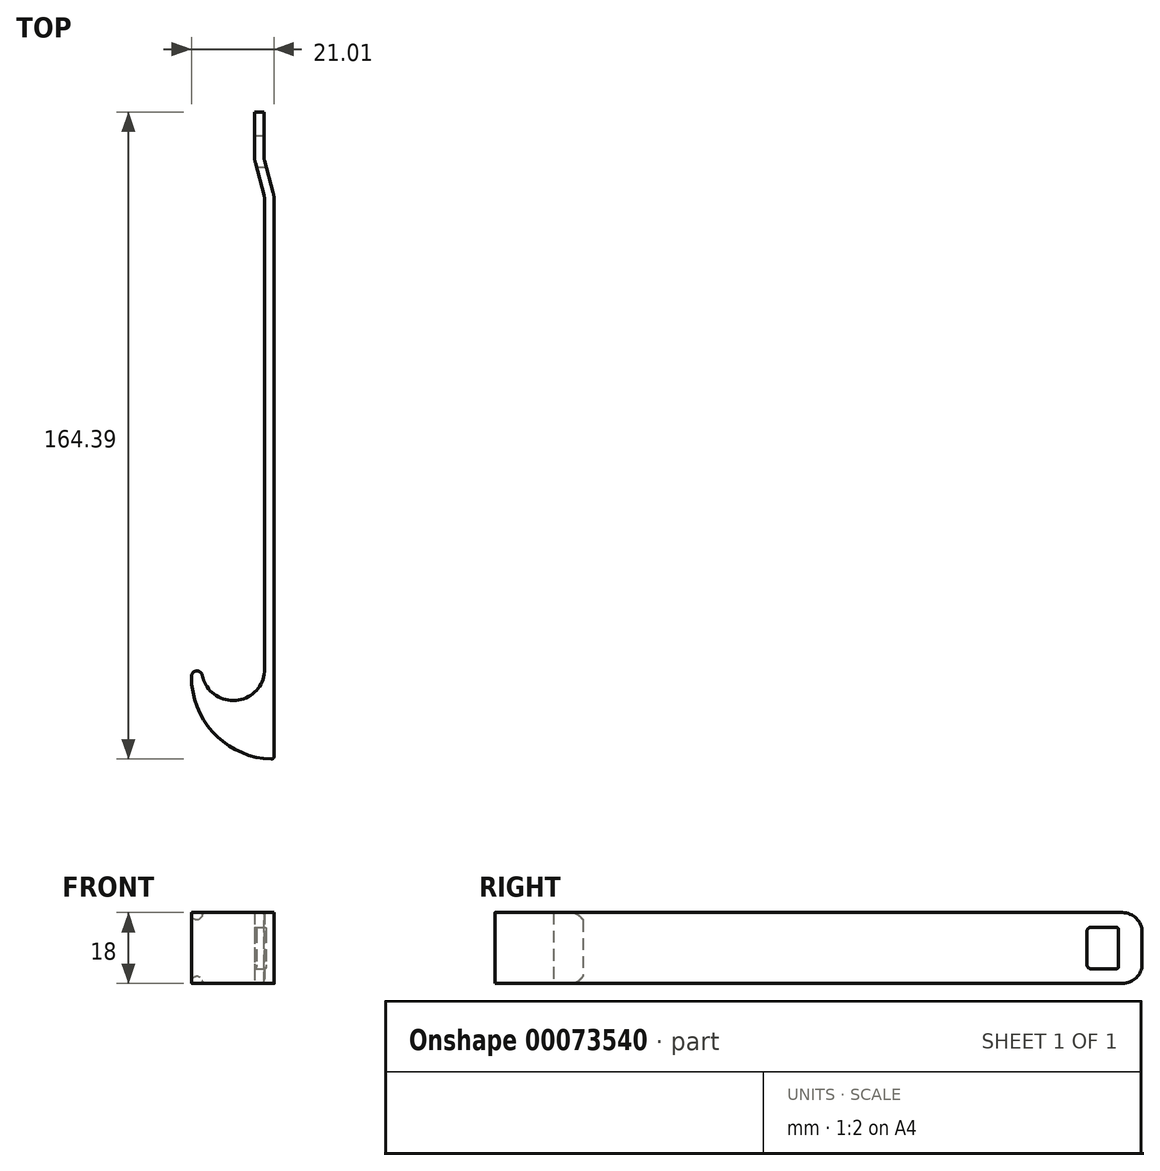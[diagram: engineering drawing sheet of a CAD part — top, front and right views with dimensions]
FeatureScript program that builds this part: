
annotation { "Feature Type Name" : "Feature", "Feature Type Description" : "" }
export const myFeature = defineFeature(function(context is Context, id is Id, definition is map)
    precondition{}
    {
        {
            var Q0;
            Q0=qCreatedBy(makeId("Top.planeOp"),FACE);
            var sketch = newSketch(context, id + "F0", { "sketchPlane" : qUnion([Q0])});
            skLineSegment(sketch, "E0", {"start": v(-2.4, -9.7) * mm, "end": v(-2.4, -129.5) * mm});
            skArc(sketch, "E1", {"start": v(-18.23, -131.12) * mm, "mid": v(-9.59, -137.46) * mm, "end": v(-2.4, -129.5) * mm});
            skLineSegment(sketch, "E2", {"start": v(-18.23, -131.12) * mm, "end": v(-10.4, -129.5) * mm, "construction": true});
            skLineSegment(sketch, "E3", {"start": v(-10.4, -129.5) * mm, "end": v(-2.4, -129.5) * mm, "construction": true});
            skArc(sketch, "E4", {"start": v(-18.23, -131.12) * mm, "mid": v(-19.75, -130) * mm, "end": v(-21, -131.4) * mm});
            skArc(sketch, "E5", {"start": v(-21, -131.4) * mm, "mid": v(-15.1, -146) * mm, "end": v(-0.72, -152.4) * mm});
            skLineSegment(sketch, "E6", {"start": v(0, -151.7) * mm, "end": v(0, -9.39) * mm});
            skLineSegment(sketch, "E7", {"start": v(-21, -131.4) * mm, "end": v(-21, -129.5) * mm, "construction": true});
            skLineSegment(sketch, "E8", {"start": v(-21, -129.5) * mm, "end": v(-10.4, -129.5) * mm, "construction": true});
            skPoint(sketch, "E9.visualSharp", {"position": v(0, -152.4) * mm});
            skArc(sketch, "E9.filletArc", {"start": v(-0.72, -152.4) * mm, "mid": v(-0.21, -152.2) * mm, "end": v(0, -151.7) * mm});
            skLineSegment(sketch, "E10", {"start": v(-21, -130) * mm, "end": v(-18.23, -130) * mm, "construction": true});
            skLineSegment(sketch, "E11", {"start": v(-18.23, -130) * mm, "end": v(-18.23, -131.12) * mm, "construction": true});
            skLineSegment(sketch, "E12", {"start": v(-5, 0) * mm, "end": v(-5, 12) * mm});
            skLineSegment(sketch, "E13", {"start": v(-5, 12) * mm, "end": v(-2.6, 12) * mm});
            skLineSegment(sketch, "E14", {"start": v(-2.6, 12) * mm, "end": v(-2.6, 0.32) * mm});
            skLineSegment(sketch, "E15", {"start": v(-0.72, -152.4) * mm, "end": v(0, -152.4) * mm, "construction": true});
            skLineSegment(sketch, "E16", {"start": v(0, -152.4) * mm, "end": v(0, -151.7) * mm, "construction": true});
            skPoint(sketch, "E17.visualSharp", {"position": v(0, 0) * mm});
            skLineSegment(sketch, "E18", {"start": v(-5, 0) * mm, "end": v(-2.4, -9.7) * mm});
            skLineSegment(sketch, "E19", {"start": v(-5, 0) * mm, "end": v(-2.52, 0) * mm, "construction": true});
            skLineSegment(sketch, "E20", {"start": v(-2.6, 0.32) * mm, "end": v(0, -9.39) * mm});
            skSolve(sketch);
        }
        {
            var Q0;
            Q0 = qSketchRegion(id + "F0", true);
            extrude(context, id + "F1", {"entities" : qUnion([Q0]), "depth" : 18 * mm, "symmetric" : true});
        }
        {
            var Q0;
            Q0=makeQuery(id+"F1.opExtrude","SWEPT_EDGE",EDGE,{"disambiguationData":[OSD([sQuery(id+"F0.wireOp",EDGE,"E0"),sQuery(id+"F0.wireOp",EDGE,"E18")])]});
            var Q1;
            Q1=makeQuery(id+"F1.opExtrude","SWEPT_EDGE",EDGE,{"disambiguationData":[OSD([sQuery(id+"F0.wireOp",EDGE,"E14"),sQuery(id+"F0.wireOp",EDGE,"E20")])]});
            fillet(context, id + "F2", {"entities" : qUnion([Q0, Q1]), "radius" : 5 * mm, "tangentPropagation" : true, "allowEdgeOverflow" : false});
        }
        {
            var Q0;
            Q0=makeQuery(id+"F1.opExtrude","SWEPT_EDGE",EDGE,{"disambiguationData":[OSD([sQuery(id+"F0.wireOp",EDGE,"E12"),sQuery(id+"F0.wireOp",EDGE,"E18")])]});
            var Q1;
            Q1=makeQuery(id+"F1.opExtrude","SWEPT_EDGE",EDGE,{"disambiguationData":[OSD([sQuery(id+"F0.wireOp",EDGE,"E6"),sQuery(id+"F0.wireOp",EDGE,"E20")])]});
            fillet(context, id + "F3", {"entities" : qUnion([Q0, Q1]), "radius" : 7.4 * mm, "tangentPropagation" : true, "allowEdgeOverflow" : false});
        }
        {
            var Q0;
            Q0=qCreatedBy(makeId("Right.planeOp"),FACE);
            var sketch = newSketch(context, id + "F4", { "sketchPlane" : qUnion([Q0])});
            skArc(sketch, "E21", {"start": v(-133.4, -9) * mm, "mid": v(-130.57, -7.83) * mm, "end": v(-129.4, -5) * mm});
            skLineSegment(sketch, "E22", {"start": v(-129.4, -5) * mm, "end": v(-129.4, 5) * mm});
            skArc(sketch, "E23", {"start": v(-129.4, 5) * mm, "mid": v(-130.57, 7.83) * mm, "end": v(-133.4, 9) * mm});
            skLineSegment(sketch, "E24", {"start": v(-133.4, -9) * mm, "end": v(-133.4, -10) * mm});
            skLineSegment(sketch, "E25", {"start": v(-133.4, -10) * mm, "end": v(-128.4, -10) * mm});
            skLineSegment(sketch, "E26", {"start": v(-128.4, -10) * mm, "end": v(-128.4, 10) * mm});
            skLineSegment(sketch, "E27", {"start": v(-128.4, 10) * mm, "end": v(-133.4, 10) * mm});
            skLineSegment(sketch, "E28", {"start": v(-133.4, 10) * mm, "end": v(-133.4, 9) * mm});
            skLineSegment(sketch, "E29", {"start": v(-133.4, -9) * mm, "end": v(-133.4, 9) * mm, "construction": true});
            skLineSegment(sketch, "E30", {"start": v(-128.4, 0) * mm, "end": v(-133.4, 0) * mm, "construction": true});
            skSolve(sketch);
        }
        {
            var Q0;
            Q0 = qSketchRegion(id + "F4", true);
            extrude(context, id + "F5", {"entities" : qUnion([Q0]), "operationType" : NewBodyOperationType.REMOVE, "oppositeDirection" : true, "depth" : 30 * mm, "hasSecondDirection" : true, "secondDirectionOppositeDirection" : true, "secondDirectionDepth" : 10 * mm});
        }
        {
            var Q0;
            Q0=qCreatedBy(makeId("Right.planeOp"),FACE);
            var sketch = newSketch(context, id + "F6", { "sketchPlane" : qUnion([Q0])});
            skLineSegment(sketch, "E31", {"start": v(6, -4.75) * mm, "end": v(6, 4.75) * mm});
            skLineSegment(sketch, "E32", {"start": v(5.5, 5.25) * mm, "end": v(-1, 5.25) * mm});
            skLineSegment(sketch, "E33", {"start": v(-2, 4.25) * mm, "end": v(-2, -4.25) * mm});
            skLineSegment(sketch, "E34", {"start": v(-1, -5.25) * mm, "end": v(5.5, -5.25) * mm});
            skLineSegment(sketch, "E35", {"start": v(-2, 0) * mm, "end": v(6, 0) * mm, "construction": true});
            skLineSegment(sketch, "E36", {"start": v(6, 5.25) * mm, "end": v(12, 5.25) * mm, "construction": true});
            skLineSegment(sketch, "E37", {"start": v(12, 5.25) * mm, "end": v(12, -5.25) * mm, "construction": true});
            skLineSegment(sketch, "E38", {"start": v(12, -5.25) * mm, "end": v(6, -5.25) * mm, "construction": true});
            skPoint(sketch, "E39.visualSharp", {"position": v(6, 5.25) * mm});
            skArc(sketch, "E39.filletArc", {"start": v(6, 4.75) * mm, "mid": v(5.85, 5.1) * mm, "end": v(5.5, 5.25) * mm});
            skPoint(sketch, "E40.visualSharp", {"position": v(6, -5.25) * mm});
            skArc(sketch, "E40.filletArc", {"start": v(5.5, -5.25) * mm, "mid": v(5.85, -5.1) * mm, "end": v(6, -4.75) * mm});
            skPoint(sketch, "E41.visualSharp", {"position": v(-2, 5.25) * mm});
            skArc(sketch, "E41.filletArc", {"start": v(-1, 5.25) * mm, "mid": v(-1.7, 4.96) * mm, "end": v(-2, 4.25) * mm});
            skPoint(sketch, "E42.visualSharp", {"position": v(-2, -5.25) * mm});
            skArc(sketch, "E42.filletArc", {"start": v(-2, -4.25) * mm, "mid": v(-1.7, -4.96) * mm, "end": v(-1, -5.25) * mm});
            skSolve(sketch);
        }
        {
            var Q0;
            Q0 = qSketchRegion(id + "F6", true);
            extrude(context, id + "F7", {"entities" : qUnion([Q0]), "operationType" : NewBodyOperationType.REMOVE, "oppositeDirection" : true, "depth" : 15 * mm});
        }
        {
            var Q0;
            Q0=makeQuery(id+"F1.opExtrude","CAP_EDGE",EDGE,{"disambiguationData":[OSD([sQuery(id+"F0.wireOp",EDGE,"E13")])],"isStart":true});
            var Q1;
            Q1=makeQuery(id+"F1.opExtrude","CAP_EDGE",EDGE,{"disambiguationData":[OSD([sQuery(id+"F0.wireOp",EDGE,"E13")])],"isStart":false});
            fillet(context, id + "F8", {"entities" : qUnion([Q0, Q1]), "radius" : 5 * mm, "tangentPropagation" : true, "allowEdgeOverflow" : false});
        }
    });
